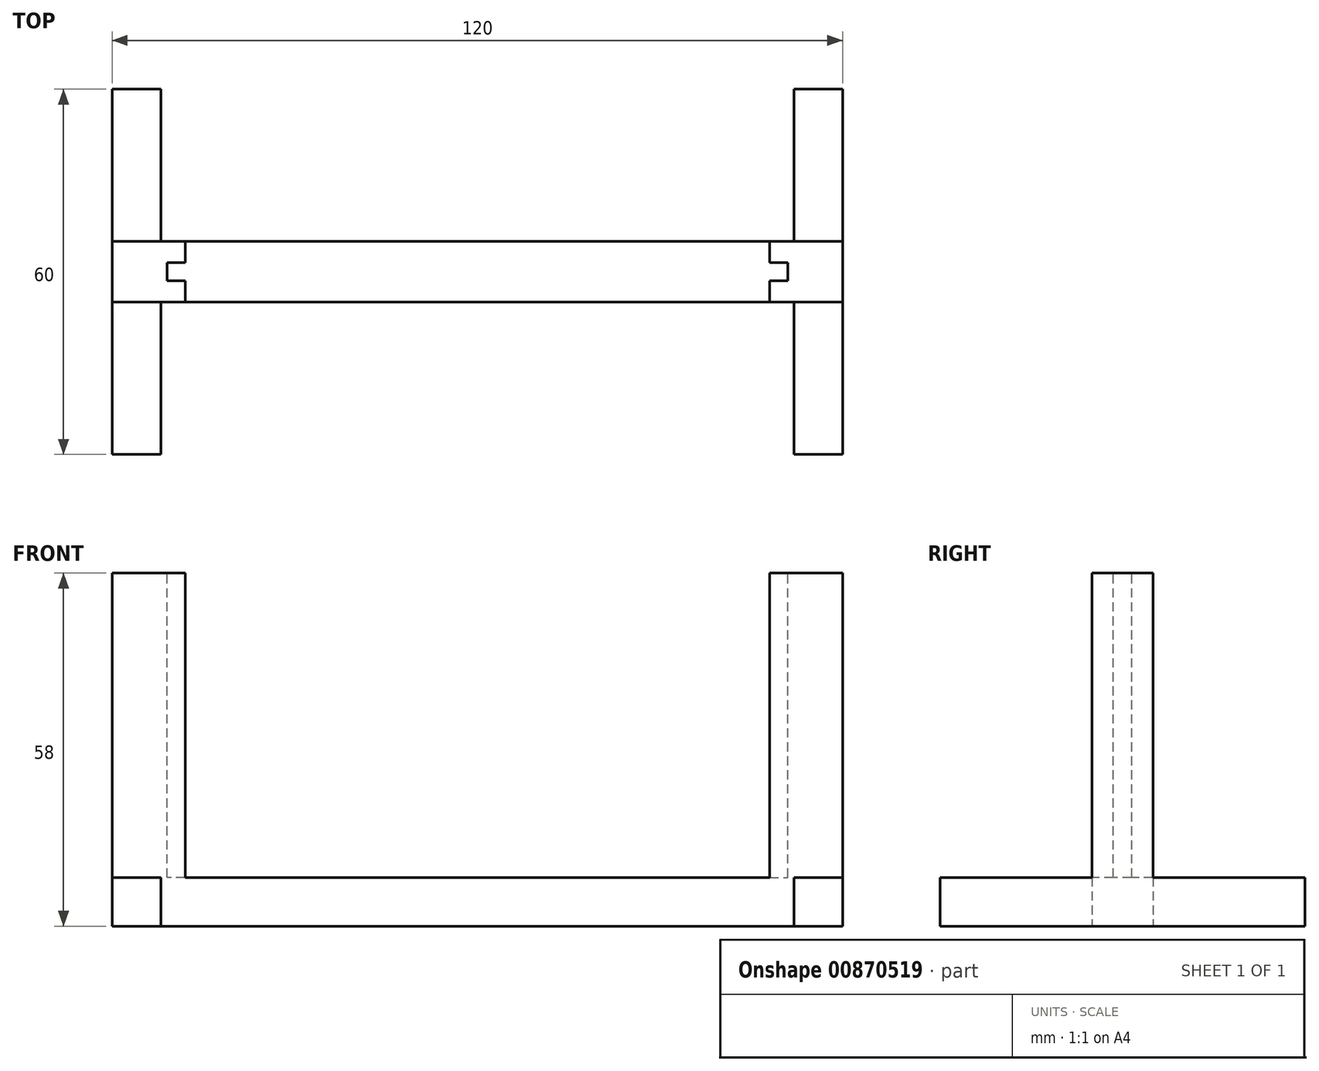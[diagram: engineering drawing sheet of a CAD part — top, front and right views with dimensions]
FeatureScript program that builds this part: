
annotation { "Feature Type Name" : "Feature", "Feature Type Description" : "" }
export const myFeature = defineFeature(function(context is Context, id is Id, definition is map)
    precondition{}
    {
        {
            var Q0;
            Q0=qCreatedBy(makeId("Top.planeOp"),FACE);
            var sketch = newSketch(context, id + "F0", { "sketchPlane" : qUnion([Q0])});
            skLineSegment(sketch, "E0.bottom", {"start": v(-60, 5) * mm, "end": v(60, 5) * mm});
            skLineSegment(sketch, "E0.top", {"start": v(-60, -5) * mm, "end": v(60, -5) * mm});
            skLineSegment(sketch, "E0.left", {"start": v(-60, 5) * mm, "end": v(-60, -5) * mm});
            skLineSegment(sketch, "E0.right", {"start": v(60, 5) * mm, "end": v(60, -5) * mm});
            skLineSegment(sketch, "E1.bottom", {"start": v(-60, -5) * mm, "end": v(-52, -5) * mm});
            skLineSegment(sketch, "E1.top", {"start": v(-60, -30) * mm, "end": v(-52, -30) * mm});
            skLineSegment(sketch, "E1.left", {"start": v(-60, -5) * mm, "end": v(-60, -30) * mm});
            skLineSegment(sketch, "E1.right", {"start": v(-52, -5) * mm, "end": v(-52, -30) * mm});
            skLineSegment(sketch, "E2.bottom", {"start": v(-60, 5) * mm, "end": v(-52, 5) * mm});
            skLineSegment(sketch, "E2.top", {"start": v(-60, 30) * mm, "end": v(-52, 30) * mm});
            skLineSegment(sketch, "E2.left", {"start": v(-60, 5) * mm, "end": v(-60, 30) * mm});
            skLineSegment(sketch, "E2.right", {"start": v(-52, 5) * mm, "end": v(-52, 30) * mm});
            skLineSegment(sketch, "E3.bottom", {"start": v(60, -5) * mm, "end": v(52, -5) * mm});
            skLineSegment(sketch, "E3.top", {"start": v(60, -30) * mm, "end": v(52, -30) * mm});
            skLineSegment(sketch, "E3.left", {"start": v(60, -5) * mm, "end": v(60, -30) * mm});
            skLineSegment(sketch, "E3.right", {"start": v(52, -5) * mm, "end": v(52, -30) * mm});
            skLineSegment(sketch, "E4.bottom", {"start": v(60, 5) * mm, "end": v(52, 5) * mm});
            skLineSegment(sketch, "E4.top", {"start": v(60, 30) * mm, "end": v(52, 30) * mm});
            skLineSegment(sketch, "E4.left", {"start": v(60, 5) * mm, "end": v(60, 30) * mm});
            skLineSegment(sketch, "E4.right", {"start": v(52, 5) * mm, "end": v(52, 30) * mm});
            skSolve(sketch);
        }
        {
            var Q0;
            Q0=makeQuery(id+"F0.imprint","IMPRINT",FACE,{"disambiguationData":[TD([[makeQuery(id+"F0.imprint","IMPRINT",EDGE,{"derivedFrom":sQuery(id+"F0.wireOp",EDGE,"E2.top")}),-1.0]])]});
            var Q1;
            Q1=makeQuery(id+"F0.imprint","IMPRINT",FACE,{"disambiguationData":[TD([[makeQuery(id+"F0.imprint","IMPRINT",EDGE,{"derivedFrom":sQuery(id+"F0.wireOp",EDGE,"E3.top")}),-1.0]])]});
            var Q2;
            Q2=makeQuery(id+"F0.imprint","IMPRINT",FACE,{"disambiguationData":[TD([[makeQuery(id+"F0.imprint","IMPRINT",EDGE,{"derivedFrom":sQuery(id+"F0.wireOp",EDGE,"E4.top")}),1.0]])]});
            var Q3;
            {var subQ7=sQuery(id+"F0.wireOp",EDGE,"E0.left");Q3=makeQuery(id+"F0.imprint","IMPRINT",FACE,{"disambiguationData":[TD([[makeQuery(id+"F0.imprint","IMPRINT",EDGE,{"derivedFrom":subQ7}),1.0]])]});}
            var Q4;
            Q4=makeQuery(id+"F0.imprint","IMPRINT",FACE,{"disambiguationData":[TD([[makeQuery(id+"F0.imprint","IMPRINT",EDGE,{"derivedFrom":sQuery(id+"F0.wireOp",EDGE,"E1.top")}),1.0]])]});
            extrude(context, id + "F1", {"entities" : qUnion([Q0, Q1, Q2, Q3, Q4]), "depth" : 8 * mm, "offsetDistance" : 25 * mm});
        }
        {
            var Q0;
            Q0=makeQuery(id+"F1.opExtrude","CAP_FACE",FACE,{"disambiguationData":[OSD([sQuery(id+"F0.wireOp",EDGE,"E0.bottom"),sQuery(id+"F0.wireOp",EDGE,"E0.top"),sQuery(id+"F0.wireOp",EDGE,"E0.left"),sQuery(id+"F0.wireOp",EDGE,"E0.right"),sQuery(id+"F0.wireOp",EDGE,"E1.top"),sQuery(id+"F0.wireOp",EDGE,"E1.left"),sQuery(id+"F0.wireOp",EDGE,"E1.right"),sQuery(id+"F0.wireOp",EDGE,"E2.top"),sQuery(id+"F0.wireOp",EDGE,"E2.left"),sQuery(id+"F0.wireOp",EDGE,"E2.right"),sQuery(id+"F0.wireOp",EDGE,"E3.top"),sQuery(id+"F0.wireOp",EDGE,"E3.left"),sQuery(id+"F0.wireOp",EDGE,"E3.right"),sQuery(id+"F0.wireOp",EDGE,"E4.top"),sQuery(id+"F0.wireOp",EDGE,"E4.left"),sQuery(id+"F0.wireOp",EDGE,"E4.right")])],"isStart":false});
            var sketch = newSketch(context, id + "F2", { "sketchPlane" : qUnion([Q0])});
            skLineSegment(sketch, "E5.bottom", {"start": v(48, 5) * mm, "end": v(60, 5) * mm});
            skLineSegment(sketch, "E5.top", {"start": v(48, -5) * mm, "end": v(60, -5) * mm});
            skLineSegment(sketch, "E5.left", {"start": v(48, 5) * mm, "end": v(48, -5) * mm});
            skLineSegment(sketch, "E5.right", {"start": v(60, 5) * mm, "end": v(60, -5) * mm});
            skSolve(sketch);
        }
        {
            var Q0;
            Q0 = qSketchRegion(id + "F2", true);
            extrude(context, id + "F3", {"entities" : qUnion([Q0]), "operationType" : NewBodyOperationType.ADD, "depth" : 50 * mm, "offsetDistance" : 25 * mm});
        }
        {
            var Q0;
            {var subQ0=sQuery(id+"F0.wireOp",EDGE,"E1.top");var subQ1=sQuery(id+"F0.wireOp",EDGE,"E2.left");var subQ2=sQuery(id+"F0.wireOp",EDGE,"E1.left");var subQ3=sQuery(id+"F0.wireOp",EDGE,"E0.left");var subQ4=sQuery(id+"F0.wireOp",EDGE,"E0.top");var subQ5=sQuery(id+"F0.wireOp",EDGE,"E0.bottom");var subQ6=sQuery(id+"F0.wireOp",EDGE,"E1.right");var subQ7=sQuery(id+"F0.wireOp",EDGE,"E2.top");var subQ8=sQuery(id+"F0.wireOp",EDGE,"E2.right");Q0=makeQuery(id+"F3.boolean.opBoolean","SPLIT",FACE,{"disambiguationData":[TD([makeQuery(id+"F1.opExtrude","SWEPT_FACE",FACE,{"disambiguationData":[OSD([subQ0])]})])],"derivedFrom":makeQuery(id+"F1.opExtrude","CAP_FACE",FACE,{"disambiguationData":[OSD([subQ5,subQ4,subQ3,sQuery(id+"F0.wireOp",EDGE,"E0.right"),subQ0,subQ2,subQ6,subQ7,subQ1,subQ8,sQuery(id+"F0.wireOp",EDGE,"E3.top"),sQuery(id+"F0.wireOp",EDGE,"E3.left"),sQuery(id+"F0.wireOp",EDGE,"E3.right"),sQuery(id+"F0.wireOp",EDGE,"E4.top"),sQuery(id+"F0.wireOp",EDGE,"E4.left"),sQuery(id+"F0.wireOp",EDGE,"E4.right")])],"isStart":false})});}
            var sketch = newSketch(context, id + "F4", { "sketchPlane" : qUnion([Q0])});
            skLineSegment(sketch, "E6.bottom", {"start": v(-60, 5) * mm, "end": v(-48, 5) * mm});
            skLineSegment(sketch, "E6.top", {"start": v(-60, -5) * mm, "end": v(-48, -5) * mm});
            skLineSegment(sketch, "E6.left", {"start": v(-60, 5) * mm, "end": v(-60, -5) * mm});
            skLineSegment(sketch, "E6.right", {"start": v(-48, 5) * mm, "end": v(-48, -5) * mm});
            skSolve(sketch);
        }
        {
            var Q0;
            Q0 = qSketchRegion(id + "F4", true);
            extrude(context, id + "F5", {"entities" : qUnion([Q0]), "operationType" : NewBodyOperationType.ADD, "depth" : 50 * mm, "offsetDistance" : 25 * mm});
        }
        {
            var Q0;
            Q0=makeQuery(id+"F5.opExtrude","CAP_FACE",FACE,{"disambiguationData":[OSD([sQuery(id+"F4.wireOp",EDGE,"E6.bottom"),sQuery(id+"F4.wireOp",EDGE,"E6.top"),sQuery(id+"F4.wireOp",EDGE,"E6.left"),sQuery(id+"F4.wireOp",EDGE,"E6.right")])],"isStart":false});
            var sketch = newSketch(context, id + "F6", { "sketchPlane" : qUnion([Q0])});
            skLineSegment(sketch, "E7.bottom", {"start": v(-48, 1.5) * mm, "end": v(-51, 1.5) * mm});
            skLineSegment(sketch, "E7.top", {"start": v(-48, -1.5) * mm, "end": v(-51, -1.5) * mm});
            skLineSegment(sketch, "E7.left", {"start": v(-48, 1.5) * mm, "end": v(-48, -1.5) * mm});
            skLineSegment(sketch, "E7.right", {"start": v(-51, 1.5) * mm, "end": v(-51, -1.5) * mm});
            skSolve(sketch);
        }
        {
            var Q0;
            Q0 = qSketchRegion(id + "F6", true);
            extrude(context, id + "F7", {"entities" : qUnion([Q0]), "operationType" : NewBodyOperationType.REMOVE, "oppositeDirection" : true, "depth" : 50 * mm, "offsetDistance" : 25 * mm});
        }
        {
            var Q0;
            Q0=makeQuery(id+"F3.opExtrude","CAP_FACE",FACE,{"disambiguationData":[OSD([sQuery(id+"F2.wireOp",EDGE,"E5.bottom"),sQuery(id+"F2.wireOp",EDGE,"E5.top"),sQuery(id+"F2.wireOp",EDGE,"E5.left"),sQuery(id+"F2.wireOp",EDGE,"E5.right")])],"isStart":false});
            var sketch = newSketch(context, id + "F8", { "sketchPlane" : qUnion([Q0])});
            skLineSegment(sketch, "E8.bottom", {"start": v(48, 1.5) * mm, "end": v(51, 1.5) * mm});
            skLineSegment(sketch, "E8.top", {"start": v(48, -1.5) * mm, "end": v(51, -1.5) * mm});
            skLineSegment(sketch, "E8.left", {"start": v(48, 1.5) * mm, "end": v(48, -1.5) * mm});
            skLineSegment(sketch, "E8.right", {"start": v(51, 1.5) * mm, "end": v(51, -1.5) * mm});
            skSolve(sketch);
        }
        {
            var Q0;
            Q0 = qSketchRegion(id + "F8", true);
            extrude(context, id + "F9", {"entities" : qUnion([Q0]), "operationType" : NewBodyOperationType.REMOVE, "oppositeDirection" : true, "depth" : 50 * mm, "offsetDistance" : 25 * mm});
        }
    });
